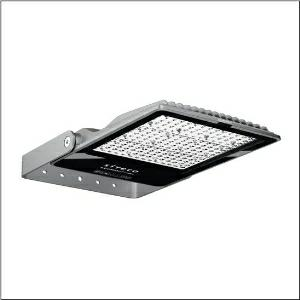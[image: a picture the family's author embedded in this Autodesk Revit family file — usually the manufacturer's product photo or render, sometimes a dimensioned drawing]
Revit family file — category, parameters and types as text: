
# Revit family: sicompact_r__31_midi___pl32_5xa7581e1k23_f752
name_source: partatom
category: Lighting Fixtures
units: mm (PartAtom-declared; Revit-internal decimal feet)

## family parameters
Cut with Voids When Loaded = No
Host = Face
Light Source = No
Part Type = Normal
Room Calculation Point = No
Round Connector Dimension = Use Diameter
Shared = No

## types (1)
- SiCompact® 31 midi  PL32 (1 x LED, 37000 lm, 250 W, 3000K)
    Apparent Load = 250 VA
    CIE Flux Codes = 32 69 98 100 100
    Color Rendering = 70
    Color Temperature = 3000K
    Default Elevation = 1800 mm
    Description = SiCompact® 31 midi, floodlight, primary light control with lens, of plastic, of toughened safety glass, transparent, light distribution: PL32, light emission: direct distribution, primary light characteristic: asymmetric, installation type: surface-mounted, LED, High Power LED, rated luminous flux: 37.000lm, luminous efficacy: 148lm/W, light colour: 730, colour temperature: 3000K, control gear: ON/OFF, with cable, 3x 1.5mm², mains connection: 220..240V, AC, 50/60Hz, connection cable pre-assembled, cable length: 2m, rated input power: 250W, of diecast aluminium, specular, metallic grey (RAL 9006), length: 560mm, width: 330mm, height: 62mm, bracket, of sheet steel, coated, metallic grey (RAL 9006), ON/OFF, protection rating (complete): IP66, insulation class (complete): insulation class I (protective earthing), certification: CE, ENEC, impact resistance: IK08, permissible operating ambient temperature: -40..+45°C, packaging unit: 1 piece

Light Distribution: PL32
    Height = 62 mm  [stored 0.203412 ft]
    Lamp = 1 x LED
    Lamp Light Flux = 37000 lm
    Lamp Power = 250 W
    Lamp count = 1
    Length = 560 mm
    Luminous efficacy = 148 lm/W
    Manufacturer = Siteco
    ModVariant = No
    Model = 5XA7581E1K23
    Mounting Place = Wall
    Mounting Type = Surface mounted
    Number of Poles = 1
    OnlyDefault = Yes
    Power Factor = 1
    Product Name = SiCompact® 31 midi | PL32
    Product group = floodlight | wall mounted
    ProductGroupID = 2001
    Protection Class = Protection class I
    Protection Degree = IP 66
    RLX_Detail_Level = 1
    RLX_Emergency_Light_Flux = 0 lm
    RLX_Emergency_Type = 0
    RLX_Emergency_Type_DB = No
    RlxData = <blob elided: 98217 chars, md5=01b83d26>
    Socket = socket
    Standby Power = 0 W
    System Light Flux = 37000 lm
    System Power = 250 W
    Type Comments = Product without accessories
    Type Image = l_1006415.jpg
    URL = http://relux.com
    VarID = ---
    Voltage = 0 V
    Weight = 0.00 kg
    Width = 333 mm

note: [stored X ft] marks values corroborated as IEEE doubles in the binary element streams (Revit-internal decimal feet)

## geometry (parser evidence)
native form markers: Blend x4, Sweep x10
no freeform markers — native parametric forms only
